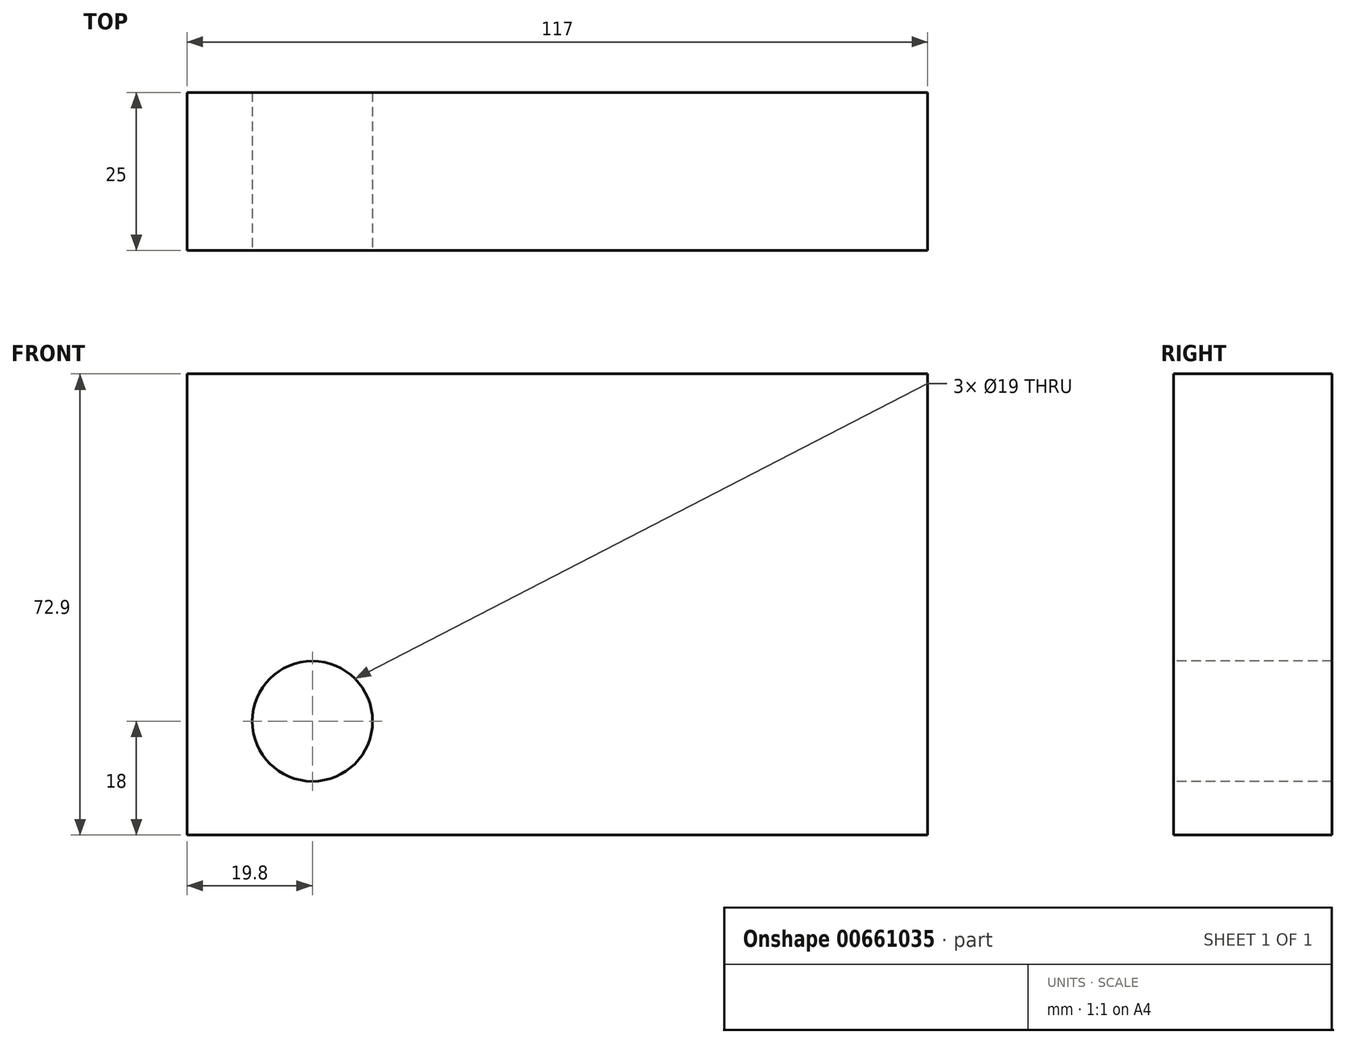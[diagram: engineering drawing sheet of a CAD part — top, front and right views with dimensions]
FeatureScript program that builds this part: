
annotation { "Feature Type Name" : "Feature", "Feature Type Description" : "" }
export const myFeature = defineFeature(function(context is Context, id is Id, definition is map)
    precondition{}
    {
        {
            var Q0;
            Q0=qCreatedBy(makeId("Front.planeOp"),FACE);
            var sketch = newSketch(context, id + "F0", { "sketchPlane" : qUnion([Q0])});
            skLineSegment(sketch, "E0.bottom", {"start": v(-59.55, 39.3) * mm, "end": v(57.45, 39.3) * mm});
            skLineSegment(sketch, "E0.top", {"start": v(-59.55, -33.6) * mm, "end": v(57.45, -33.6) * mm});
            skLineSegment(sketch, "E0.left", {"start": v(-59.55, 39.3) * mm, "end": v(-59.55, -33.6) * mm});
            skLineSegment(sketch, "E0.right", {"start": v(57.45, 39.3) * mm, "end": v(57.45, -33.6) * mm});
            skSolve(sketch);
        }
        {
            var Q0;
            Q0 = qSketchRegion(id + "F0", true);
            extrude(context, id + "F1", {"entities" : qUnion([Q0]), "depth" : 25 * mm, "offsetDistance" : 25 * mm});
        }
        {
            var Q0;
            Q0=makeQuery(id+"F1.opExtrude","SWEPT_EDGE",EDGE,{"disambiguationData":[OSD([sQuery(id+"F0.wireOp",EDGE,"E0.bottom"),sQuery(id+"F0.wireOp",EDGE,"E0.right")])]});
            cPlane(context, id + "F2", {"entities" : qUnion([Q0]), "cplaneType" : CPlaneType.LINE_ANGLE, "offset" : 25 * mm, "angle" : 45 * degree, "width" : 150 * mm, "height" : 150 * mm});
        }
        {
            var Q0;
            Q0=qCreatedBy(id+"F2.planeOp",FACE);
            var sketch = newSketch(context, id + "F3", { "sketchPlane" : qUnion([Q0])});
            skPoint(sketch, "E1", {"position": v(13.14, -14.14) * mm});
            skSolve(sketch);
        }
        {
            var Q0;
            Q0=sQuery(id+"F3.wireOp",VERTEX,"E1");
            var Q1;
            Q1=makeQuery(id+"F1.opExtrude","SWEPT_BODY",BODY,{"disambiguationData":[OSD([sQuery(id+"F0.wireOp",EDGE,"E0.bottom"),sQuery(id+"F0.wireOp",EDGE,"E0.top"),sQuery(id+"F0.wireOp",EDGE,"E0.left"),sQuery(id+"F0.wireOp",EDGE,"E0.right")])]});
            hole(context, id + "F4", {"style" : HoleStyle.SIMPLE, "endStyle" : HoleEndStyle.THROUGH, "holeDiameter" : 5.5 * mm, "majorDiameter" : 5 * mm, "isTappedThrough" : true, "tappedDepth" : 12 * mm, "tapClearance" : 3, "startFromSketch" : true, "locations" : qUnion([Q0]), "scope" : qUnion([Q1])});
        }
        {
            var Q0;
            Q0=makeQuery(id+"F1.opExtrude","CAP_FACE",FACE,{"disambiguationData":[OSD([sQuery(id+"F0.wireOp",EDGE,"E0.bottom"),sQuery(id+"F0.wireOp",EDGE,"E0.top"),sQuery(id+"F0.wireOp",EDGE,"E0.left"),sQuery(id+"F0.wireOp",EDGE,"E0.right")])],"isStart":false});
            var sketch = newSketch(context, id + "F5", { "sketchPlane" : qUnion([Q0])});
            skCircle(sketch, "E2", {"center": v(-39.75, -15.6) * mm, "radius": 9.5 * mm});
            skSolve(sketch);
        }
        {
            var Q0;
            Q0 = qSketchRegion(id + "F5", true);
            extrude(context, id + "F6", {"entities" : qUnion([Q0]), "operationType" : NewBodyOperationType.REMOVE, "oppositeDirection" : true, "depth" : 40 * mm, "offsetDistance" : 25 * mm});
        }
    });
